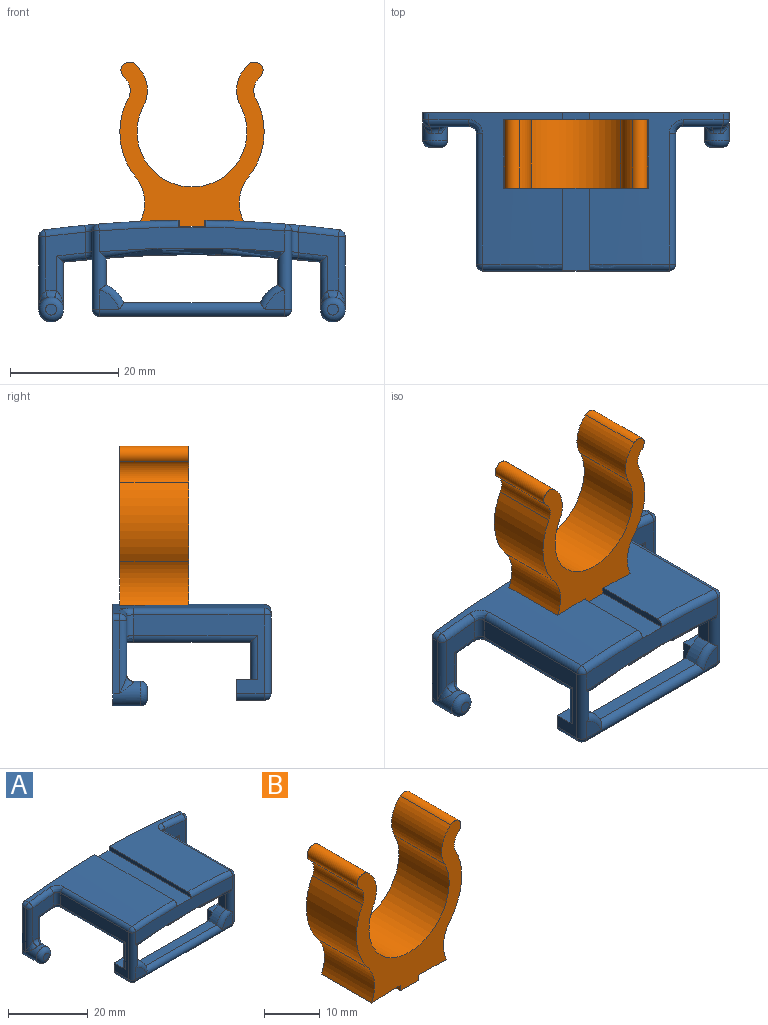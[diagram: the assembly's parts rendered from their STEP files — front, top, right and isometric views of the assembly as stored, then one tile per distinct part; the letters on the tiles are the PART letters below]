
ASSEMBLY  parts=2 mates=1
PART A: 82 faces, bbox 56.6x29.2x19 mm
  f0: cylinder r=209.55mm len=27.94mm, axis (0,1,0), area 425.7mm2, adj f2,f22,f62,f71,f74,f75,f81
  f1: torus R=208.28mm, axis (0,-1,0), area 29.3mm2, adj f3,f7,f68,f79,f80
  f2: torus R=208.28mm, axis (0,-1,0), area 29.3mm2, adj f0,f3,f73,f80,f81
  f3: plane 34.29x4.53mm, normal (0,-1,0), area 130.8mm2, adj f1,f2,f51,f60,f67
  f4: plane 3.65x3.65mm, normal (0,-1,0), area 9.1mm2, adj f49,f50,f51
  f5: plane 24.13x14.53mm, normal (1,0,0), area 115.5mm2, adj f11,f26,f57,f58,f65,f67,f72,f75
  f6: plane 3.81x3.81mm, normal (0,1,0), area 14.2mm2, adj f8,f9,f24,f25,f45
  f7: cylinder r=209.55mm len=27.94mm, axis (0,1,0), area 425.7mm2, adj f1,f22,f42,f47,f54,f61,f79
  f8: plane 24.13x14.53mm, normal (-1,0,0), area 115.5mm2, adj f6,f25,f36,f39,f45,f46,f51,f61
  f9: plane 34.29x5.08mm, normal (0,0,-1), area 62.9mm2, adj f6,f11,f24,f27,f45,f50,f58,f76
  f10: plane 3.65x3.65mm, normal (0,-1,0), area 9.1mm2, adj f50,f59,f67
  f11: plane 3.81x3.81mm, normal (0,1,0), area 14.2mm2, adj f5,f9,f26,f27,f58
  f12: cylinder r=203.2mm len=47.5mm, axis (0,-1,0), area 967.2mm2, adj f18,f21,f22,f28,f29,f31,f39,f40
  f13: plane 10.9x7.37mm, normal (0,-1,0), area 41mm2, adj f48,f56,f63,f64,f71,f72
  f14: cylinder r=2.29mm len=5.08mm, axis (0,1,0), area 51.1mm2, adj f18,f19,f22,f34,f35,f38,f78
  f15: plane 2.03x2.03mm, normal (0,-1,0), area 3.2mm2, adj f78
  f16: cylinder r=2.29mm len=5.08mm, axis (0,1,0), area 51.1mm2, adj f20,f21,f22,f48,f52,f55,f77
  f17: plane 2.03x2.03mm, normal (0,-1,0), area 3.2mm2, adj f77
  f18: plane 8.77x1.27mm, normal (1,0,0), area 11.1mm2, adj f12,f14,f22,f37
  f19: plane 13.48x1.27mm, normal (-1,0,0), area 17.1mm2, adj f14,f22,f41,f42
  f20: plane 13.48x1.27mm, normal (1,0,0), area 17.1mm2, adj f16,f22,f62,f63
  f21: plane 8.77x1.27mm, normal (-1,0,0), area 11.1mm2, adj f12,f16,f22,f56
  f22: plane 56.64x18.78mm, normal (0,1,0), area 447.9mm2, adj f0,f7,f12,f14,f16,f18,f19,f20
  f23: plane 10.9x7.37mm, normal (0,-1,0), area 41mm2, adj f35,f37,f40,f41,f46,f47
  f24: plane 3.81x3.81mm, normal (1,0,0), area 10mm2, adj f6,f9,f25,f28,f76
  f25: plane 3.81x3.81mm, normal (0,0,1), area 10mm2, adj f6,f8,f24,f28,f36
  f26: plane 3.81x3.81mm, normal (0,0,1), area 10mm2, adj f5,f11,f27,f28,f57
  f27: plane 3.81x3.81mm, normal (-1,0,0), area 10mm2, adj f9,f11,f26,f28,f76
  f28: plane 34.29x9.54mm, normal (0,1,0), area 65mm2, adj f12,f24,f25,f26,f27,f29,f30,f31
  f29: plane 4.99x2.54mm, normal (-1,0,0), area 12.7mm2, adj f12,f28,f30,f67
  f30: cylinder r=6.35mm len=3.28mm, axis (0,1,0), area 12.1mm2, adj f28,f29,f32,f59
  f31: plane 4.99x2.54mm, normal (1,0,0), area 12.7mm2, adj f12,f28,f33,f51
  f32: plane 25.19x2.54mm, normal (0,0,1), area 64mm2, adj f28,f30,f33,f50
  f33: cylinder r=6.35mm len=3.28mm, axis (0,1,0), area 12.1mm2, adj f28,f31,f32,f49
  f34: bspline ~3.41x2.54mm, area 3.7mm2, adj f14,f35,f37
  f35: torus R=3.56mm, axis (0,1,0), area 3.2mm2, adj f14,f23,f34,f38
  f36: cylinder r=1.27mm len=8.17mm, axis (0,0,1), area 14.7mm2, adj f8,f25,f28,f39
  f37: cylinder r=1.27mm len=9.89mm, axis (0,0,-1), area 14.3mm2, adj f18,f23,f34,f40
  f38: bspline ~3.41x2.54mm, area 3.7mm2, adj f14,f35,f41
  f39: cylinder r=1.27mm len=22.86mm, axis (0,-1,0), area 46.3mm2, adj f8,f12,f28,f36,f43
  f40: torus R=204.47mm, axis (0,1,0), area 9.2mm2, adj f12,f23,f37,f43
  f41: cylinder r=1.27mm len=13.48mm, axis (0,0,1), area 22.9mm2, adj f19,f23,f38,f44
  f42: cylinder r=1.27mm len=1.27mm, axis (0,1,0), area 2.3mm2, adj f7,f19,f22,f44
  f43: bspline ~3.11x2.95mm, area 5.6mm2, adj f12,f39,f40,f46
  f44: sphere r=1.27mm, area 2.3mm2, adj f41,f42,f47
  f45: cylinder r=1.27mm len=5.08mm, axis (0,1,0), area 10.1mm2, adj f6,f8,f9,f53
  f46: cylinder r=1.27mm len=4.05mm, axis (0,0,1), area 7.6mm2, adj f8,f23,f43,f54
  f47: torus R=208.28mm, axis (0,1,0), area 14.8mm2, adj f7,f23,f44,f54
  f48: torus R=3.56mm, axis (0,1,0), area 3.2mm2, adj f13,f16,f52,f55
  f49: torus R=5.08mm, axis (0,-1,0), area 10mm2, adj f4,f33,f50,f51
  f50: cylinder r=1.27mm len=34.29mm, axis (1,0,0), area 119.9mm2, adj f4,f9,f10,f32,f49,f53,f59,f66
  f51: cylinder r=1.27mm len=14.53mm, axis (0,0,-1), area 40.4mm2, adj f3,f4,f8,f31,f49,f53,f60,f68
  f52: bspline ~3.41x2.54mm, area 3.7mm2, adj f16,f48,f56
  f53: sphere r=1.27mm, area 2.5mm2, adj f45,f50,f51
  f54: bspline ~3.13x2.98mm, area 5.3mm2, adj f7,f46,f47,f61
  f55: bspline ~3.41x2.54mm, area 3.7mm2, adj f16,f48,f63
  f56: cylinder r=1.27mm len=9.89mm, axis (0,0,1), area 14.3mm2, adj f13,f21,f52,f64
  f57: cylinder r=1.27mm len=8.17mm, axis (0,0,-1), area 14.7mm2, adj f5,f26,f28,f65
  f58: cylinder r=1.27mm len=5.08mm, axis (0,-1,0), area 10.1mm2, adj f5,f9,f11,f66
  f59: torus R=5.08mm, axis (0,-1,0), area 10mm2, adj f10,f30,f50,f67
  f60: torus R=204.47mm, axis (0,-1,0), area 65.2mm2, adj f3,f12,f51,f67
  f61: cylinder r=1.27mm len=24.13mm, axis (0,1,0), area 45.6mm2, adj f7,f8,f54,f68
  f62: cylinder r=1.27mm len=1.27mm, axis (0,1,0), area 2.3mm2, adj f0,f20,f22,f69
  f63: cylinder r=1.27mm len=13.48mm, axis (0,0,-1), area 22.9mm2, adj f13,f20,f55,f69
  f64: torus R=204.47mm, axis (0,1,0), area 9.2mm2, adj f12,f13,f56,f70
  f65: cylinder r=1.27mm len=22.86mm, axis (0,-1,0), area 46.3mm2, adj f5,f12,f28,f57,f70
  f66: sphere r=1.27mm, area 2.5mm2, adj f50,f58,f67
  f67: cylinder r=1.27mm len=14.53mm, axis (0,0,1), area 40.4mm2, adj f3,f5,f10,f29,f59,f60,f66,f73
  f68: sphere r=1.27mm, area 2.4mm2, adj f1,f51,f61
  f69: sphere r=1.27mm, area 2.3mm2, adj f62,f63,f71
  f70: bspline ~2.98x2.72mm, area 5.6mm2, adj f12,f64,f65,f72
  f71: torus R=208.28mm, axis (0,1,0), area 14.8mm2, adj f0,f13,f69,f74
  f72: cylinder r=1.27mm len=4.05mm, axis (0,0,-1), area 7.6mm2, adj f5,f13,f70,f74
  f73: sphere r=1.27mm, area 2.4mm2, adj f2,f67,f75
  f74: bspline ~3.11x2.99mm, area 5.3mm2, adj f0,f71,f72,f75
  f75: cylinder r=1.27mm len=24.13mm, axis (0,1,0), area 45.6mm2, adj f0,f5,f73,f74
  f76: cylinder r=1.27mm len=29.21mm, axis (-1,0,0), area 58.3mm2, adj f9,f24,f27,f28
  f77: torus R=1.02mm, axis (0,1,0), area 22.9mm2, adj f16,f17
  f78: torus R=1.02mm, axis (0,1,0), area 22.9mm2, adj f14,f15
  f79: plane 29.22x1.26mm, normal (1,0,0), area 36.3mm2, adj f1,f7,f22,f80
  f80: plane 29.22x5.09mm, normal (0,0,1), area 148.4mm2, adj f1,f2,f22,f79,f81
  f81: plane 29.22x1.26mm, normal (-1,0,0), area 36.3mm2, adj f0,f2,f22,f80
PART B: 18 faces, bbox 26.7x12.7x30.4 mm
  f0: cylinder r=3.17mm len=12.7mm, axis (0,1,0), area 54.7mm2, adj f1,f15,f16,f17
  f1: cylinder r=1.59mm len=12.7mm, axis (0,1,0), area 63.3mm2, adj f0,f2,f16,f17
  f2: cylinder r=6.35mm len=12.7mm, axis (0,1,0), area 109.5mm2, adj f1,f3,f16,f17
  f3: cylinder r=10.16mm len=20.32mm, axis (0,1,0), area 530.6mm2, adj f2,f4,f16,f17
  f4: cylinder r=6.35mm len=12.7mm, axis (0,1,0), area 109.5mm2, adj f3,f5,f16,f17
  f5: cylinder r=1.59mm len=12.7mm, axis (0,1,0), area 63.3mm2, adj f4,f6,f16,f17
  f6: cylinder r=3.17mm len=12.7mm, axis (0,1,0), area 54.7mm2, adj f5,f7,f16,f17
  f7: cylinder r=13.33mm len=14.56mm, axis (0,1,0), area 196.7mm2, adj f6,f8,f16,f17
  f8: cylinder r=7.62mm len=12.7mm, axis (0,1,0), area 110.2mm2, adj f7,f9,f16,f17
  f9: cylinder r=209.55mm len=12.7mm, axis (0,1,0), area 92mm2, adj f8,f10,f16,f17
  f10: plane 12.7x1.13mm, normal (-1,0,0), area 14.4mm2, adj f9,f11,f16,f17
  f11: plane 12.7x4.57mm, normal (0,0,-1), area 58.1mm2, adj f10,f12,f16,f17
  f12: plane 12.7x1.13mm, normal (1,0,0), area 14.4mm2, adj f11,f13,f16,f17
  f13: cylinder r=209.55mm len=12.7mm, axis (0,1,0), area 92mm2, adj f12,f14,f16,f17
  f14: cylinder r=7.62mm len=12.7mm, axis (0,1,0), area 110.2mm2, adj f13,f15,f16,f17
  f15: cylinder r=13.33mm len=14.56mm, axis (0,1,0), area 196.7mm2, adj f0,f14,f16,f17
  f16: plane 30.37x26.67mm, normal (0,-1,0), area 281.8mm2, adj f0,f1,f2,f3,f4,f5,f6,f7
  f17: plane 30.37x26.67mm, normal (0,1,0), area 281.8mm2, adj f0,f1,f2,f3,f4,f5,f6,f7
PLACE A t=(0,3.45,0)mm
PLACE B t=(0,25.04,23.48)mm
MATE fastened A.f0 <-> B.f9  axis (0,1,0) through (0,12.34,-202.36)mm
